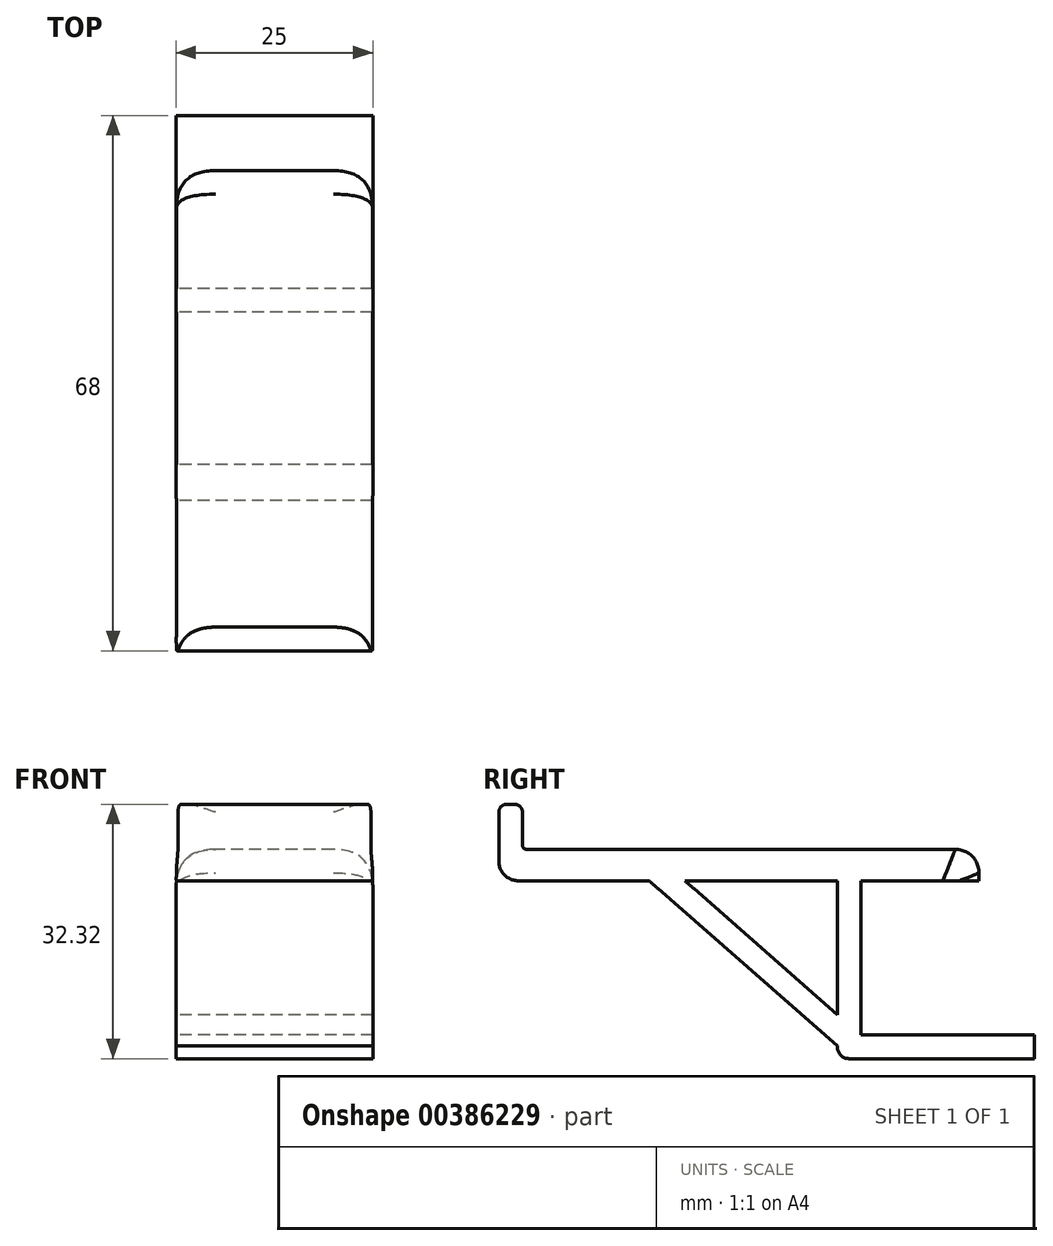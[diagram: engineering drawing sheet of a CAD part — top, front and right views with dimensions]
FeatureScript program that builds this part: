
annotation { "Feature Type Name" : "Feature", "Feature Type Description" : "" }
export const myFeature = defineFeature(function(context is Context, id is Id, definition is map)
    precondition{}
    {
        {
            var Q0;
            Q0=qCreatedBy(makeId("Right.planeOp"),FACE);
            var sketch = newSketch(context, id + "F0", { "sketchPlane" : qUnion([Q0])});
            skLineSegment(sketch, "E0", {"start": v(-64.5, 1.62) * mm, "end": v(-10, 1.62) * mm});
            skLineSegment(sketch, "E1", {"start": v(-7, -1.38) * mm, "end": v(-7, -2.38) * mm});
            skLineSegment(sketch, "E2", {"start": v(-68, 0.12) * mm, "end": v(-68, 6.34) * mm});
            skLineSegment(sketch, "E3", {"start": v(-67, 7.34) * mm, "end": v(-66, 7.34) * mm});
            skLineSegment(sketch, "E4", {"start": v(-65, 6.34) * mm, "end": v(-65, 2.12) * mm});
            skPoint(sketch, "E5.visualSharp", {"position": v(-65, 1.62) * mm});
            skPoint(sketch, "E6.visualSharp", {"position": v(-65, 7.34) * mm});
            skArc(sketch, "E6.filletArc", {"start": v(-65, 6.34) * mm, "mid": v(-65.3, 7.04) * mm, "end": v(-66, 7.34) * mm});
            skPoint(sketch, "E7.visualSharp", {"position": v(-68, 7.34) * mm});
            skArc(sketch, "E7.filletArc", {"start": v(-67, 7.34) * mm, "mid": v(-67.7, 7.04) * mm, "end": v(-68, 6.34) * mm});
            skArc(sketch, "E8.filletArc", {"start": v(-68, -1.96) * mm, "mid": v(-68, -1.97) * mm, "end": v(-68, -1.98) * mm});
            skLineSegment(sketch, "E9", {"start": v(-7, -2.38) * mm, "end": v(-22, -2.38) * mm});
            skLineSegment(sketch, "E10", {"start": v(-22, -2.38) * mm, "end": v(-22, -21.98) * mm});
            skLineSegment(sketch, "E11", {"start": v(-22, -21.98) * mm, "end": v(0, -21.98) * mm});
            skLineSegment(sketch, "E12", {"start": v(0, -21.98) * mm, "end": v(0, -24.98) * mm});
            skLineSegment(sketch, "E13", {"start": v(0, -24.98) * mm, "end": v(-23.5, -24.98) * mm});
            skLineSegment(sketch, "E14", {"start": v(-25, -23.48) * mm, "end": v(-25, -23.38) * mm});
            skPoint(sketch, "E15.visualSharp", {"position": v(-25, -24.98) * mm});
            skArc(sketch, "E15.filletArc", {"start": v(-25, -23.48) * mm, "mid": v(-24.56, -24.54) * mm, "end": v(-23.5, -24.98) * mm});
            skArc(sketch, "E16.filletArc", {"start": v(-65, 2.12) * mm, "mid": v(-64.85, 1.77) * mm, "end": v(-64.5, 1.62) * mm});
            skPoint(sketch, "E17.visualSharp", {"position": v(-7, 1.62) * mm});
            skArc(sketch, "E17.filletArc", {"start": v(-7, -1.38) * mm, "mid": v(-7.88, 0.74) * mm, "end": v(-10, 1.62) * mm});
            skArc(sketch, "E18.filletArc", {"start": v(-68, 0.12) * mm, "mid": v(-67.27, -1.65) * mm, "end": v(-65.5, -2.38) * mm});
            skLineSegment(sketch, "E19", {"start": v(-65.5, -2.38) * mm, "end": v(-48.92, -2.38) * mm});
            skLineSegment(sketch, "E20", {"start": v(-25, -19.39) * mm, "end": v(-25, -2.38) * mm});
            skLineSegment(sketch, "E21", {"start": v(-25, -23.38) * mm, "end": v(-48.92, -2.38) * mm});
            skLineSegment(sketch, "E22", {"start": v(-44.37, -2.38) * mm, "end": v(-25, -19.39) * mm});
            skLineSegment(sketch, "E23.trimOffspring", {"start": v(-44.37, -2.38) * mm, "end": v(-25, -2.38) * mm});
            skSolve(sketch);
        }
        {
            var Q0;
            Q0=makeQuery(id+"F0.imprint","IMPRINT",FACE,{"disambiguationData":[TD([[makeQuery(id+"F0.imprint","IMPRINT",EDGE,{"derivedFrom":sQuery(id+"F0.wireOp",EDGE,"E0")}),-1.0]])]});
            extrude(context, id + "F1", {"entities" : qUnion([Q0]), "depth" : 25 * mm});
        }
        {
            var Q0;
            Q0=makeQuery(id+"F1.opExtrude","CAP_EDGE",EDGE,{"disambiguationData":[OSD([sQuery(id+"F0.wireOp",EDGE,"E0")])],"isStart":false});
            var Q1;
            Q1=makeQuery(id+"F1.opExtrude","CAP_EDGE",EDGE,{"disambiguationData":[OSD([sQuery(id+"F0.wireOp",EDGE,"E0")])],"isStart":true});
            fillet(context, id + "F2", {"entities" : qUnion([Q0, Q1]), "radius" : 5 * mm, "tangentPropagation" : true, "rho" : 0.5, "crossSection" : FilletCrossSection.CONIC, "allowEdgeOverflow" : false});
        }
    });
